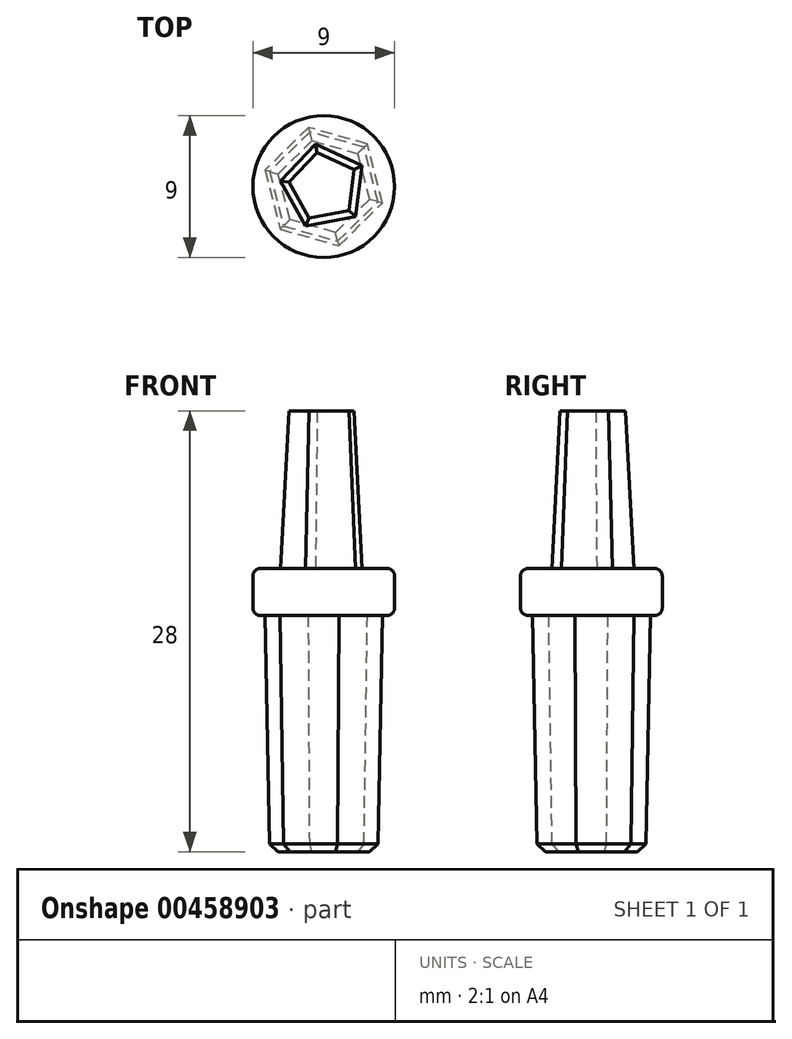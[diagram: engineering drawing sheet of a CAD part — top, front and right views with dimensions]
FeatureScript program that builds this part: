
annotation { "Feature Type Name" : "Feature", "Feature Type Description" : "" }
export const myFeature = defineFeature(function(context is Context, id is Id, definition is map)
    precondition{}
    {
        {
            var Q0;
            Q0=qCreatedBy(makeId("Top.planeOp"),FACE);
            var sketch = newSketch(context, id + "F0", { "sketchPlane" : qUnion([Q0])});
            skCircle(sketch, "E0.cCircle", {"center": v(0, 0) * mm, "radius": 2.76 * mm, "construction": true});
            skLineSegment(sketch, "E0.0", {"start": v(2.02, -1.89) * mm, "end": v(-1.17, -2.5) * mm});
            skLineSegment(sketch, "E0.1", {"start": v(-1.17, -2.5) * mm, "end": v(-2.74, 0.34) * mm});
            skLineSegment(sketch, "E0.2", {"start": v(-2.74, 0.34) * mm, "end": v(-0.52, 2.71) * mm});
            skLineSegment(sketch, "E0.3", {"start": v(-0.52, 2.71) * mm, "end": v(2.42, 1.33) * mm});
            skLineSegment(sketch, "E0.4", {"start": v(2.42, 1.33) * mm, "end": v(2.02, -1.89) * mm});
            skSolve(sketch);
        }
        {
            var Q0;
            Q0=makeQuery(id+"F0.imprint","IMPRINT",FACE,{"disambiguationData":[TD([[makeQuery(id+"F0.imprint","IMPRINT",EDGE,{"derivedFrom":sQuery(id+"F0.wireOp",EDGE,"E0.0")}),-1.0]])]});
            extrude(context, id + "F1", {"entities" : qUnion([Q0]), "depth" : 10 * mm, "hasDraft" : true, "draftAngle" : 2.56 * degree, "draftPullDirection" : true});
        }
        {
            var Q0;
            Q0=qCreatedBy(makeId("Top.planeOp"),FACE);
            var sketch = newSketch(context, id + "F2", { "sketchPlane" : qUnion([Q0])});
            skCircle(sketch, "E1", {"center": v(0, 0) * mm, "radius": 4.5 * mm});
            skSolve(sketch);
        }
        {
            var Q0;
            Q0=makeQuery(id+"F2.imprint","IMPRINT",FACE,{"disambiguationData":[TD([[makeQuery(id+"F2.imprint","IMPRINT",EDGE,{"derivedFrom":sQuery(id+"F2.wireOp",EDGE,"E1")}),1.0]])]});
            extrude(context, id + "F3", {"entities" : qUnion([Q0]), "operationType" : NewBodyOperationType.ADD, "oppositeDirection" : true, "depth" : 3 * mm});
        }
        {
            var Q0;
            Q0=makeQuery(id+"F3.opExtrude","CAP_EDGE",EDGE,{"disambiguationData":[OSD([sQuery(id+"F2.wireOp",EDGE,"E1")])],"isStart":true});
            var Q1;
            Q1=makeQuery(id+"F3.opExtrude","CAP_EDGE",EDGE,{"disambiguationData":[OSD([sQuery(id+"F2.wireOp",EDGE,"E1")])],"isStart":false});
            fillet(context, id + "F4", {"entities" : qUnion([Q0, Q1]), "radius" : 0.5 * mm, "tangentPropagation" : true, "allowEdgeOverflow" : false});
        }
        {
            var Q0;
            Q0=makeQuery(id+"F3.opExtrude","CAP_FACE",FACE,{"disambiguationData":[OSD([sQuery(id+"F2.wireOp",EDGE,"E1")])],"isStart":false});
            var sketch = newSketch(context, id + "F5", { "sketchPlane" : qUnion([Q0])});
            skCircle(sketch, "E2.cCircle", {"center": v(0, 0) * mm, "radius": 3.35 * mm, "construction": true});
            skLineSegment(sketch, "E2.0", {"start": v(3.73, 1.05) * mm, "end": v(2.77, -2.7) * mm});
            skLineSegment(sketch, "E2.1", {"start": v(2.77, -2.7) * mm, "end": v(-0.96, -3.75) * mm});
            skLineSegment(sketch, "E2.2", {"start": v(-0.96, -3.75) * mm, "end": v(-3.73, -1.05) * mm});
            skLineSegment(sketch, "E2.3", {"start": v(-3.73, -1.05) * mm, "end": v(-2.77, 2.7) * mm});
            skLineSegment(sketch, "E2.4", {"start": v(-2.77, 2.7) * mm, "end": v(0.96, 3.75) * mm});
            skLineSegment(sketch, "E2.5", {"start": v(0.96, 3.75) * mm, "end": v(3.73, 1.05) * mm});
            skPoint(sketch, "E2.0.midPoint", {"position": v(3.25, -0.83) * mm});
            skSolve(sketch);
        }
        {
            var Q0;
            Q0 = qSketchRegion(id + "F5", true);
            extrude(context, id + "F6", {"entities" : qUnion([Q0]), "operationType" : NewBodyOperationType.ADD, "depth" : 15 * mm, "hasDraft" : true, "draftAngle" : 1 * degree, "draftPullDirection" : true});
        }
        {
            var Q0;
            Q0=makeQuery(id+"F6.opExtrude","CAP_EDGE",EDGE,{"disambiguationData":[OSD([sQuery(id+"F5.wireOp",EDGE,"E2.5")])],"isStart":false});
            var Q1;
            Q1=makeQuery(id+"F6.opExtrude","CAP_EDGE",EDGE,{"disambiguationData":[OSD([sQuery(id+"F5.wireOp",EDGE,"E2.4")])],"isStart":false});
            var Q2;
            Q2=makeQuery(id+"F6.opExtrude","CAP_EDGE",EDGE,{"disambiguationData":[OSD([sQuery(id+"F5.wireOp",EDGE,"E2.3")])],"isStart":false});
            var Q3;
            Q3=makeQuery(id+"F6.opExtrude","CAP_EDGE",EDGE,{"disambiguationData":[OSD([sQuery(id+"F5.wireOp",EDGE,"E2.2")])],"isStart":false});
            var Q4;
            Q4=makeQuery(id+"F6.opExtrude","CAP_EDGE",EDGE,{"disambiguationData":[OSD([sQuery(id+"F5.wireOp",EDGE,"E2.1")])],"isStart":false});
            var Q5;
            Q5=makeQuery(id+"F6.opExtrude","CAP_EDGE",EDGE,{"disambiguationData":[OSD([sQuery(id+"F5.wireOp",EDGE,"E2.0")])],"isStart":false});
            chamfer(context, id + "F7", {"entities" : qUnion([Q0, Q1, Q2, Q3, Q4, Q5]), "width" : 0.5 * mm, "tangentPropagation" : true});
        }
    });
